# Revit family: Sink-Vessel-Lavatory-KOHLER-Vox-K-30673_
name_source: partatom
category: Plumbing Fixtures
units: mm (PartAtom-declared; Revit-internal decimal feet)

## family parameters
Cut with Voids When Loaded = No
Host = Face
OmniClass Number = 23.31.13.00
OmniClass Title = Sinks
Part Type = Normal
Room Calculation Point = No
Round Connector Dimension = Use Diameter
Shared = No

## types (2) — shared parameters
ADA Compliant = No
Assembly Code = D2010400
CW Connection = No
Cold Water Inlet = Cold Water Inlet
Date Modified = 01/25/2024
Default Elevation = 36"
Description = 21-3/4 Inch rectangular vessel bathroom sink, no overflow
Drain Included = No
HW Connection = No
Height = 6 1/8"
Hot Water Inlet = Hot Water Inlet
Length = 23"
Manufacturer = Kohler Co.
Master Format 2014 = 22 41 16
Master Format 2014 Name = Residential Lavatories and Sinks
Material = Vitreous China
Product Documentation Link = https://www.us.kohler.com
Product Name = Vox
Product Page URL = http://www.us.kohler.com
URL = https://www.us.kohler.com
Vent Connection = No
Waste Connection = Yes
Waste Water Outlet = Waste Water Outlet
WaterSense Certified = No
Width = 16 5/16"

## per-type parameters (varying)
| type | Finish | Model | Type |
| AHN-Ashen | KOHLER-Vitreous_China-AHN-Ashen | K-30673-N-AHN | 1 |
| EGS-Eggshell | KOHLER-Vitreous_China-EGS-Eggshell | K-30673-N-EGS | 2 |

## geometry (parser evidence)
native form markers: Sweep x5
no freeform markers — native parametric forms only
